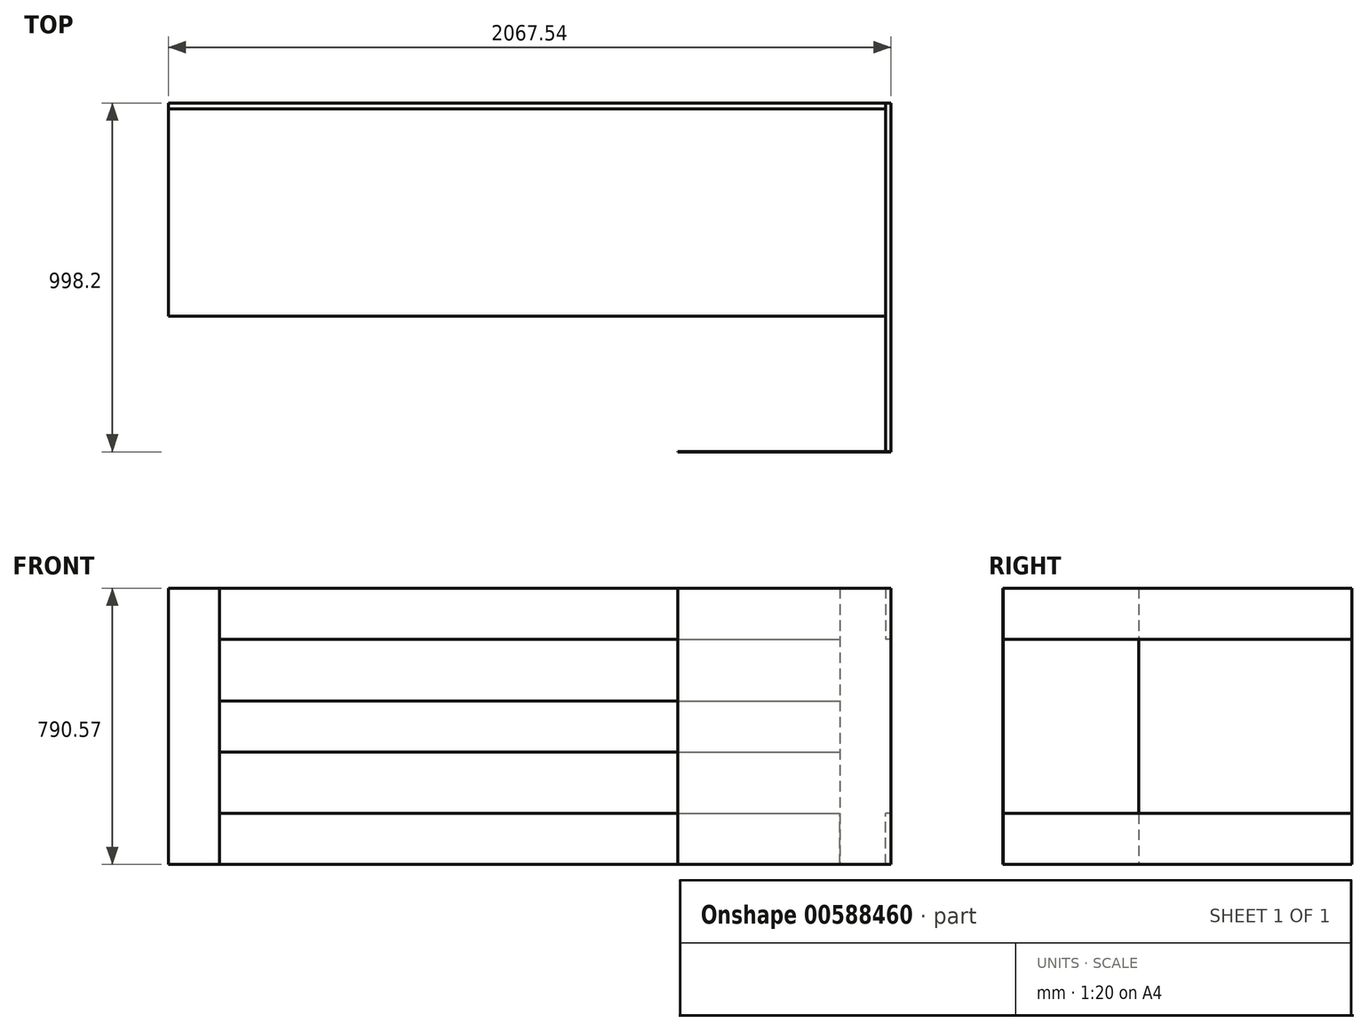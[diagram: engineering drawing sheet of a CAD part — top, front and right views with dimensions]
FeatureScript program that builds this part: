
annotation { "Feature Type Name" : "Feature", "Feature Type Description" : "" }
export const myFeature = defineFeature(function(context is Context, id is Id, definition is map)
    precondition{}
    {
        {
            assignVariable(context, id + "F0", {"name" : "thick", "anyValue" : 0.62});
        }
        {
            var Q0;
            Q0=qCreatedBy(makeId("Front.planeOp"),FACE);
            var sketch = newSketch(context, id + "F1", { "sketchPlane" : qUnion([Q0])});
            skLineSegment(sketch, "E0.bottom", {"start": v(0, 21.43) * mm, "end": v(146.05, 21.43) * mm});
            skLineSegment(sketch, "E0.top", {"start": v(0, 812) * mm, "end": v(146.05, 812) * mm});
            skLineSegment(sketch, "E0.left", {"start": v(0, 21.43) * mm, "end": v(0, 812) * mm});
            skLineSegment(sketch, "E0.right", {"start": v(146.05, 21.43) * mm, "end": v(146.05, 812) * mm});
            skLineSegment(sketch, "E1.bottom", {"start": v(146.05, 812) * mm, "end": v(1920.88, 812) * mm});
            skLineSegment(sketch, "E1.top", {"start": v(146.05, 665.95) * mm, "end": v(1920.88, 665.95) * mm});
            skLineSegment(sketch, "E1.left", {"start": v(146.05, 812) * mm, "end": v(146.05, 665.95) * mm});
            skLineSegment(sketch, "E1.right", {"start": v(1920.88, 812) * mm, "end": v(1920.88, 665.95) * mm});
            skLineSegment(sketch, "E2.bottom", {"start": v(146.05, 21.43) * mm, "end": v(1920.88, 21.43) * mm});
            skLineSegment(sketch, "E2.top", {"start": v(146.05, 167.48) * mm, "end": v(1920.88, 167.48) * mm});
            skLineSegment(sketch, "E2.left", {"start": v(146.05, 21.43) * mm, "end": v(146.05, 167.48) * mm});
            skLineSegment(sketch, "E2.right", {"start": v(1920.88, 21.43) * mm, "end": v(1920.88, 167.48) * mm});
            skLineSegment(sketch, "E3.bottom", {"start": v(1920.88, 812) * mm, "end": v(2066.92, 812) * mm});
            skLineSegment(sketch, "E3.top", {"start": v(1920.88, 21.43) * mm, "end": v(2066.92, 21.43) * mm});
            skLineSegment(sketch, "E3.left", {"start": v(1920.88, 812) * mm, "end": v(1920.88, 21.43) * mm});
            skLineSegment(sketch, "E3.right", {"start": v(2066.92, 812) * mm, "end": v(2066.92, 21.43) * mm});
            skPoint(sketch, "E4", {"position": v(146.05, 489.74) * mm});
            skPoint(sketch, "E5", {"position": v(146.05, 343.7) * mm});
            skPoint(sketch, "E6", {"position": v(1920.88, 343.7) * mm});
            skPoint(sketch, "E7", {"position": v(1936.75, 489.74) * mm});
            skPoint(sketch, "E8.end.orphan", {"position": v(1920.88, 416.72) * mm});
            skPoint(sketch, "E8.start.orphan", {"position": v(146.05, 416.72) * mm});
            skLineSegment(sketch, "E9.bottom", {"start": v(146.05, 489.74) * mm, "end": v(1920.88, 489.74) * mm});
            skLineSegment(sketch, "E9.top", {"start": v(146.05, 343.7) * mm, "end": v(1920.88, 343.7) * mm});
            skLineSegment(sketch, "E9.left", {"start": v(146.05, 489.74) * mm, "end": v(146.05, 343.7) * mm});
            skLineSegment(sketch, "E9.right", {"start": v(1920.88, 489.74) * mm, "end": v(1920.88, 343.7) * mm});
            skSolve(sketch);
        }
        {
            var Q0;
            Q0=makeQuery(id+"F1.imprint","IMPRINT",FACE,{"disambiguationData":[TD([[makeQuery(id+"F1.imprint","IMPRINT",EDGE,{"derivedFrom":sQuery(id+"F1.wireOp",EDGE,"E0.bottom")}),1.0]])]});
            extrude(context, id + "F2", {"entities" : qUnion([Q0]), "depth" : (getVariable(context, 'thick')) * mm, "offsetDistance" : 25.4 * mm});
        }
        {
            var Q0;
            {var subQ0=sQuery(id+"F1.wireOp",EDGE,"E1.bottom");Q0=makeQuery(id+"F1.imprint","IMPRINT",FACE,{"disambiguationData":[TD([[makeQuery(id+"F1.imprint","IMPRINT",EDGE,{"derivedFrom":subQ0}),-1.0]])]});}
            extrude(context, id + "F3", {"entities" : qUnion([Q0]), "depth" : (getVariable(context, 'thick')) * mm, "offsetDistance" : 25.4 * mm});
        }
        {
            var Q0;
            Q0=makeQuery(id+"F1.imprint","IMPRINT",FACE,{"disambiguationData":[TD([[makeQuery(id+"F1.imprint","IMPRINT",EDGE,{"derivedFrom":sQuery(id+"F1.wireOp",EDGE,"E9.bottom")}),-1.0]])]});
            extrude(context, id + "F4", {"entities" : qUnion([Q0]), "depth" : (getVariable(context, 'thick')) * mm, "offsetDistance" : 25.4 * mm});
        }
        {
            var Q0;
            {var subQ0=sQuery(id+"F1.wireOp",EDGE,"E2.bottom");Q0=makeQuery(id+"F1.imprint","IMPRINT",FACE,{"disambiguationData":[TD([[makeQuery(id+"F1.imprint","IMPRINT",EDGE,{"derivedFrom":subQ0}),1.0]])]});}
            extrude(context, id + "F5", {"entities" : qUnion([Q0]), "depth" : (getVariable(context, 'thick')) * mm, "offsetDistance" : 25.4 * mm});
        }
        {
            var Q0;
            {var subQ3=sQuery(id+"F1.wireOp",EDGE,"E3.bottom");Q0=makeQuery(id+"F1.imprint","IMPRINT",FACE,{"disambiguationData":[TD([[makeQuery(id+"F1.imprint","IMPRINT",EDGE,{"derivedFrom":subQ3}),-1.0]])]});}
            extrude(context, id + "F6", {"entities" : qUnion([Q0]), "depth" : (getVariable(context, 'thick')) * mm, "offsetDistance" : 25.4 * mm});
        }
        {
            var Q0;
            Q0=makeQuery(id+"F2.opExtrude","SWEPT_FACE",FACE,{"disambiguationData":[OSD([sQuery(id+"F1.wireOp",EDGE,"E0.left")])]});
            var sketch = newSketch(context, id + "F7", { "sketchPlane" : qUnion([Q0])});
            skLineSegment(sketch, "E10.bottom", {"start": v(0, 812) * mm, "end": v(609.6, 812) * mm});
            skLineSegment(sketch, "E10.top", {"start": v(0, 21.43) * mm, "end": v(609.6, 21.43) * mm});
            skLineSegment(sketch, "E10.left", {"start": v(0, 812) * mm, "end": v(0, 21.43) * mm});
            skLineSegment(sketch, "E10.right", {"start": v(609.6, 812) * mm, "end": v(609.6, 21.43) * mm});
            skSolve(sketch);
        }
        {
            var Q0;
            Q0 = qSketchRegion(id + "F7", true);
            extrude(context, id + "F8", {"entities" : qUnion([Q0]), "depth" : (getVariable(context, 'thick')) * mm, "offsetDistance" : 25.4 * mm});
        }
        {
            var Q0;
            Q0=makeQuery(id+"F6.opExtrude","CAP_FACE",FACE,{"disambiguationData":[OSD([sQuery(id+"F1.wireOp",EDGE,"E3.bottom"),sQuery(id+"F1.wireOp",EDGE,"E3.top"),sQuery(id+"F1.wireOp",EDGE,"E3.left"),sQuery(id+"F1.wireOp",EDGE,"E3.right"),sQuery(id+"F1.wireOp",EDGE,"E9.right")])],"isStart":false});
            var sketch = newSketch(context, id + "F9", { "sketchPlane" : qUnion([Q0])});
            skLineSegment(sketch, "E11.bottom", {"start": v(2066.92, 812) * mm, "end": v(2051.05, 812) * mm});
            skLineSegment(sketch, "E11.top", {"start": v(2066.92, 665.95) * mm, "end": v(2051.05, 665.95) * mm});
            skLineSegment(sketch, "E11.left", {"start": v(2066.92, 812) * mm, "end": v(2066.92, 665.95) * mm});
            skLineSegment(sketch, "E11.right", {"start": v(2051.05, 812) * mm, "end": v(2051.05, 665.95) * mm});
            skLineSegment(sketch, "E12.bottom", {"start": v(2066.92, 21.43) * mm, "end": v(2051.05, 21.43) * mm});
            skLineSegment(sketch, "E12.top", {"start": v(2066.92, 167.48) * mm, "end": v(2051.05, 167.48) * mm});
            skLineSegment(sketch, "E12.left", {"start": v(2066.92, 21.43) * mm, "end": v(2066.92, 167.48) * mm});
            skLineSegment(sketch, "E12.right", {"start": v(2051.05, 21.43) * mm, "end": v(2051.05, 167.48) * mm});
            skSolve(sketch);
        }
        {
            var Q0;
            Q0=makeQuery(id+"F9.imprint","IMPRINT",FACE,{"disambiguationData":[TD([[makeQuery(id+"F9.imprint","IMPRINT",EDGE,{"derivedFrom":sQuery(id+"F9.wireOp",EDGE,"E11.bottom")}),-1.0]])]});
            var Q1;
            Q1=makeQuery(id+"F9.imprint","IMPRINT",FACE,{"disambiguationData":[TD([[makeQuery(id+"F9.imprint","IMPRINT",EDGE,{"derivedFrom":sQuery(id+"F9.wireOp",EDGE,"E12.bottom")}),1.0]])]});
            extrude(context, id + "F10", {"entities" : qUnion([Q0, Q1]), "depth" : 996.95 * mm, "offsetDistance" : 25.4 * mm});
        }
        {
            var Q0;
            Q0=makeQuery(id+"F10.opExtrude","CAP_FACE",FACE,{"disambiguationData":[OSD([sQuery(id+"F9.wireOp",EDGE,"E11.bottom"),sQuery(id+"F9.wireOp",EDGE,"E11.top"),sQuery(id+"F9.wireOp",EDGE,"E11.left"),sQuery(id+"F9.wireOp",EDGE,"E11.right")])],"isStart":false});
            var sketch = newSketch(context, id + "F11", { "sketchPlane" : qUnion([Q0])});
            skLineSegment(sketch, "E13.bottom", {"start": v(2066.92, 812) * mm, "end": v(1457.33, 812) * mm});
            skLineSegment(sketch, "E13.top", {"start": v(2066.92, 21.43) * mm, "end": v(1457.33, 21.43) * mm});
            skLineSegment(sketch, "E13.left", {"start": v(2066.92, 812) * mm, "end": v(2066.92, 21.43) * mm});
            skLineSegment(sketch, "E13.right", {"start": v(1457.33, 812) * mm, "end": v(1457.33, 21.43) * mm});
            skSolve(sketch);
        }
        {
            var Q0;
            Q0 = qSketchRegion(id + "F11", true);
            extrude(context, id + "F12", {"entities" : qUnion([Q0]), "depth" : (getVariable(context, 'thick')) * mm, "offsetDistance" : 25.4 * mm});
        }
        {
            var Q0;
            Q0=makeQuery(id+"F8.opExtrude","SWEPT_FACE",FACE,{"disambiguationData":[OSD([sQuery(id+"F7.wireOp",EDGE,"E10.top")])]});
            var sketch = newSketch(context, id + "F13", { "sketchPlane" : qUnion([Q0])});
            skLineSegment(sketch, "E14.bottom", {"start": v(0, 609.6) * mm, "end": v(2050.83, 609.6) * mm});
            skLineSegment(sketch, "E14.top", {"start": v(0, 16.3) * mm, "end": v(2050.83, 16.3) * mm});
            skLineSegment(sketch, "E14.left", {"start": v(0, 609.6) * mm, "end": v(0, 16.3) * mm});
            skLineSegment(sketch, "E14.right", {"start": v(2050.83, 609.6) * mm, "end": v(2050.83, 16.3) * mm});
            skSolve(sketch);
        }
        {
            var Q0;
            Q0=makeQuery(id+"F13.imprint","IMPRINT",FACE,{"disambiguationData":[TD([[makeQuery(id+"F13.imprint","IMPRINT",EDGE,{"derivedFrom":sQuery(id+"F13.wireOp",EDGE,"E14.bottom")}),-1.0]])]});
            extrude(context, id + "F14", {"entities" : qUnion([Q0]), "oppositeDirection" : true, "depth" : (getVariable(context, 'thick')) * mm, "offsetDistance" : 25.4 * mm});
        }
    });
